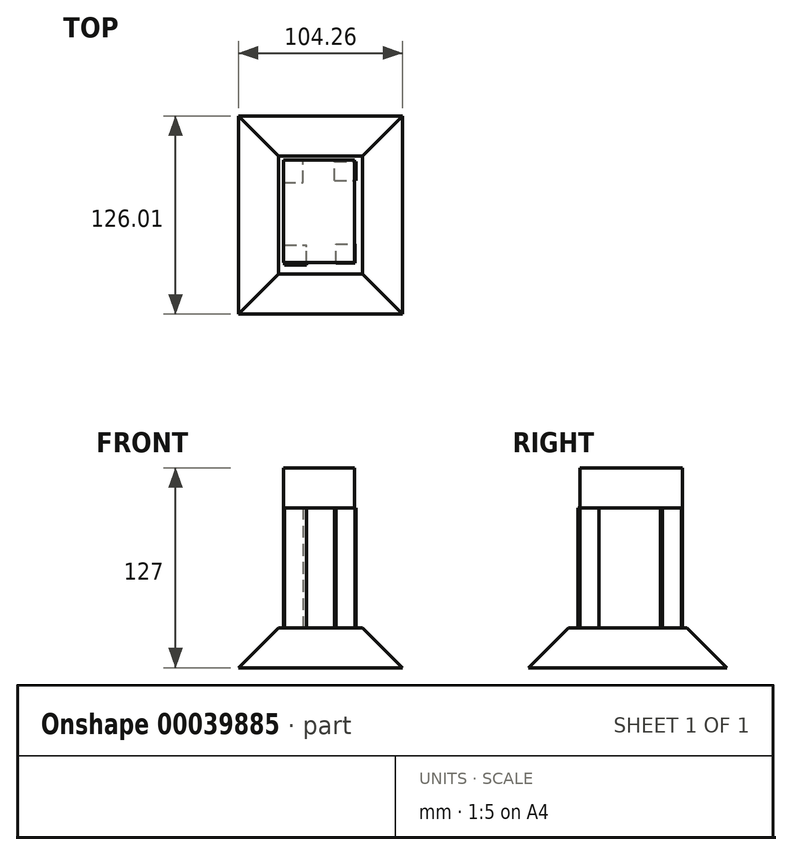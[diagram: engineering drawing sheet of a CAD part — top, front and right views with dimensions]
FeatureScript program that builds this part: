
annotation { "Feature Type Name" : "Feature", "Feature Type Description" : "" }
export const myFeature = defineFeature(function(context is Context, id is Id, definition is map)
    precondition{}
    {
        {
            var Q0;
            Q0=qCreatedBy(makeId("Top.planeOp"),FACE);
            var sketch = newSketch(context, id + "F0", { "sketchPlane" : qUnion([Q0])});
            skLineSegment(sketch, "E0.bottom", {"start": v(-47.53, -64.4) * mm, "end": v(56.73, -64.4) * mm});
            skLineSegment(sketch, "E0.top", {"start": v(-47.53, 61.61) * mm, "end": v(56.73, 61.61) * mm});
            skLineSegment(sketch, "E0.left", {"start": v(-47.53, -64.4) * mm, "end": v(-47.53, 61.61) * mm});
            skLineSegment(sketch, "E0.right", {"start": v(56.73, -64.4) * mm, "end": v(56.73, 61.61) * mm});
            skSolve(sketch);
        }
        {
            var Q0;
            Q0=makeQuery(id+"F0.imprint","IMPRINT",FACE,{"disambiguationData":[TD([[makeQuery(id+"F0.imprint","IMPRINT",EDGE,{"derivedFrom":sQuery(id+"F0.wireOp",EDGE,"E0.bottom")}),1.0]])]});
            extrude(context, id + "F1", {"entities" : qUnion([Q0]), "depth" : 25.4 * mm});
        }
        {
            var Q0;
            Q0=makeQuery(id+"F1.opExtrude","CAP_FACE",FACE,{"disambiguationData":[OSD([sQuery(id+"F0.wireOp",EDGE,"E0.bottom"),sQuery(id+"F0.wireOp",EDGE,"E0.top"),sQuery(id+"F0.wireOp",EDGE,"E0.left"),sQuery(id+"F0.wireOp",EDGE,"E0.right")])],"isStart":false});
            chamfer(context, id + "F2", {"entities" : qUnion([Q0]), "width" : 25.4 * mm, "tangentPropagation" : true});
        }
        {
            var Q0;
            Q0=makeQuery(id+"F1.opExtrude","CAP_FACE",FACE,{"disambiguationData":[OSD([sQuery(id+"F0.wireOp",EDGE,"E0.bottom"),sQuery(id+"F0.wireOp",EDGE,"E0.top"),sQuery(id+"F0.wireOp",EDGE,"E0.left"),sQuery(id+"F0.wireOp",EDGE,"E0.right")])],"isStart":false});
            var sketch = newSketch(context, id + "F3", { "sketchPlane" : qUnion([Q0])});
            skLineSegment(sketch, "E1.bottom", {"start": v(-18.82, 19.24) * mm, "end": v(-6.55, 19.24) * mm});
            skLineSegment(sketch, "E1.top", {"start": v(-18.82, 33.45) * mm, "end": v(-6.55, 33.45) * mm});
            skLineSegment(sketch, "E1.left", {"start": v(-18.82, 19.24) * mm, "end": v(-18.82, 33.45) * mm});
            skLineSegment(sketch, "E1.right", {"start": v(-6.55, 19.24) * mm, "end": v(-6.55, 33.45) * mm});
            skLineSegment(sketch, "E2.bottom", {"start": v(13.52, 20.63) * mm, "end": v(27.18, 20.63) * mm});
            skLineSegment(sketch, "E2.top", {"start": v(13.52, 32.62) * mm, "end": v(27.18, 32.62) * mm});
            skLineSegment(sketch, "E2.left", {"start": v(13.52, 20.63) * mm, "end": v(13.52, 32.62) * mm});
            skLineSegment(sketch, "E2.right", {"start": v(27.18, 20.63) * mm, "end": v(27.18, 32.62) * mm});
            skLineSegment(sketch, "E3.bottom", {"start": v(-18.26, -33.17) * mm, "end": v(-4.32, -33.17) * mm});
            skLineSegment(sketch, "E3.top", {"start": v(-18.26, -20.35) * mm, "end": v(-4.32, -20.35) * mm});
            skLineSegment(sketch, "E3.left", {"start": v(-18.26, -33.17) * mm, "end": v(-18.26, -20.35) * mm});
            skLineSegment(sketch, "E3.right", {"start": v(-4.32, -33.17) * mm, "end": v(-4.32, -20.35) * mm});
            skLineSegment(sketch, "E4.bottom", {"start": v(14.36, -31.78) * mm, "end": v(26.34, -31.78) * mm});
            skLineSegment(sketch, "E4.top", {"start": v(14.36, -19.8) * mm, "end": v(26.34, -19.8) * mm});
            skLineSegment(sketch, "E4.left", {"start": v(14.36, -31.78) * mm, "end": v(14.36, -19.8) * mm});
            skLineSegment(sketch, "E4.right", {"start": v(26.34, -31.78) * mm, "end": v(26.34, -19.8) * mm});
            skSolve(sketch);
        }
        {
            var Q0;
            Q0 = qSketchRegion(id + "F3", true);
            extrude(context, id + "F4", {"entities" : qUnion([Q0]), "operationType" : NewBodyOperationType.ADD, "depth" : 76.2 * mm});
        }
        {
            var Q0;
            Q0=makeQuery(id+"F4.opExtrude","CAP_FACE",FACE,{"disambiguationData":[OSD([sQuery(id+"F3.wireOp",EDGE,"E1.bottom"),sQuery(id+"F3.wireOp",EDGE,"E1.top"),sQuery(id+"F3.wireOp",EDGE,"E1.left"),sQuery(id+"F3.wireOp",EDGE,"E1.right")])],"isStart":false});
            var sketch = newSketch(context, id + "F5", { "sketchPlane" : qUnion([Q0])});
            skLineSegment(sketch, "E5.bottom", {"start": v(-18.82, 33.45) * mm, "end": v(26.1, 33.45) * mm});
            skLineSegment(sketch, "E5.top", {"start": v(-18.82, -31.64) * mm, "end": v(26.1, -31.64) * mm});
            skLineSegment(sketch, "E5.left", {"start": v(-18.82, 33.45) * mm, "end": v(-18.82, -31.64) * mm});
            skLineSegment(sketch, "E5.right", {"start": v(26.1, 33.45) * mm, "end": v(26.1, -31.64) * mm});
            skSolve(sketch);
        }
        {
            var Q0;
            Q0 = qSketchRegion(id + "F5", true);
            extrude(context, id + "F6", {"entities" : qUnion([Q0]), "operationType" : NewBodyOperationType.ADD, "depth" : 25.4 * mm});
        }
    });
